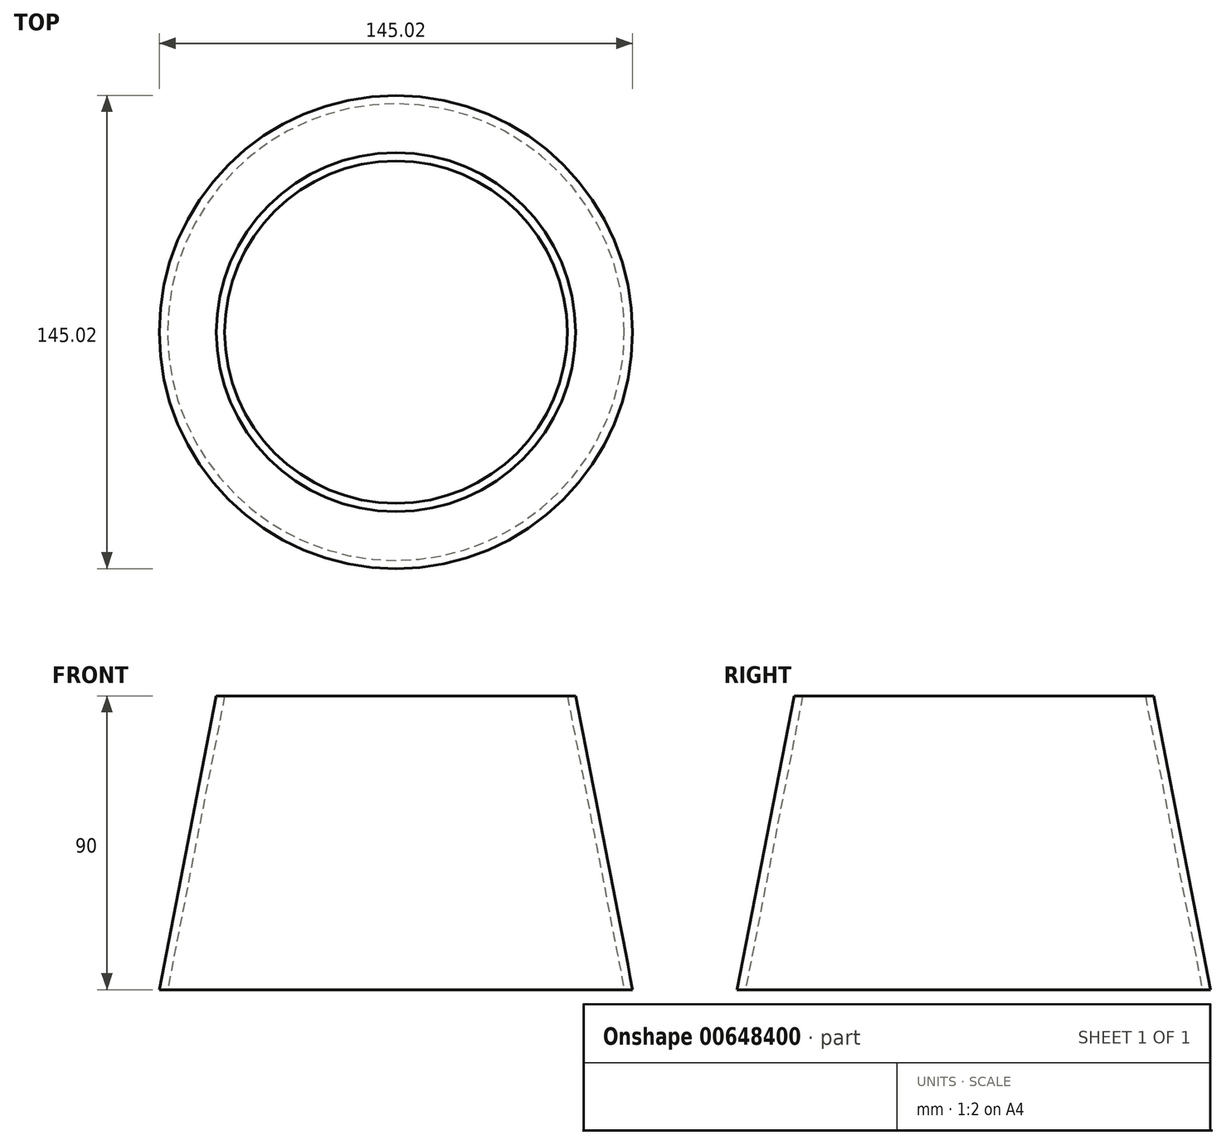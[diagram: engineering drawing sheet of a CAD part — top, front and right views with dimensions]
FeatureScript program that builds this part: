
annotation { "Feature Type Name" : "Feature", "Feature Type Description" : "" }
export const myFeature = defineFeature(function(context is Context, id is Id, definition is map)
    precondition{}
    {
        {
            var Q0;
            Q0=qCreatedBy(makeId("Top.planeOp"),FACE);
            var sketch = newSketch(context, id + "F0", { "sketchPlane" : qUnion([Q0])});
            skCircle(sketch, "E0", {"center": v(0, 0) * mm, "radius": 72.5 * mm});
            skSolve(sketch);
        }
        {
            var Q0;
            Q0=makeQuery(id+"F0.imprint","IMPRINT",FACE,{"disambiguationData":[TD([[makeQuery(id+"F0.imprint","IMPRINT",EDGE,{"derivedFrom":sQuery(id+"F0.wireOp",EDGE,"E0")}),1.0]])]});
            extrude(context, id + "F1", {"entities" : qUnion([Q0]), "depth" : 90 * mm, "offsetDistance" : 25 * mm, "hasDraft" : true, "draftAngle" : 11 * degree, "draftPullDirection" : true});
        }
        {
            var Q0;
            Q0=makeQuery(id+"F1.opExtrude","CAP_FACE",FACE,{"disambiguationData":[OSD([sQuery(id+"F0.wireOp",EDGE,"E0")])],"isStart":false});
            var Q1;
            Q1=makeQuery(id+"F1.opExtrude","CAP_FACE",FACE,{"disambiguationData":[OSD([sQuery(id+"F0.wireOp",EDGE,"E0")])],"isStart":true});
            shell(context, id + "F2", {"entities" : qUnion([Q0, Q1]), "thickness" : 2.5 * mm});
        }
    });
